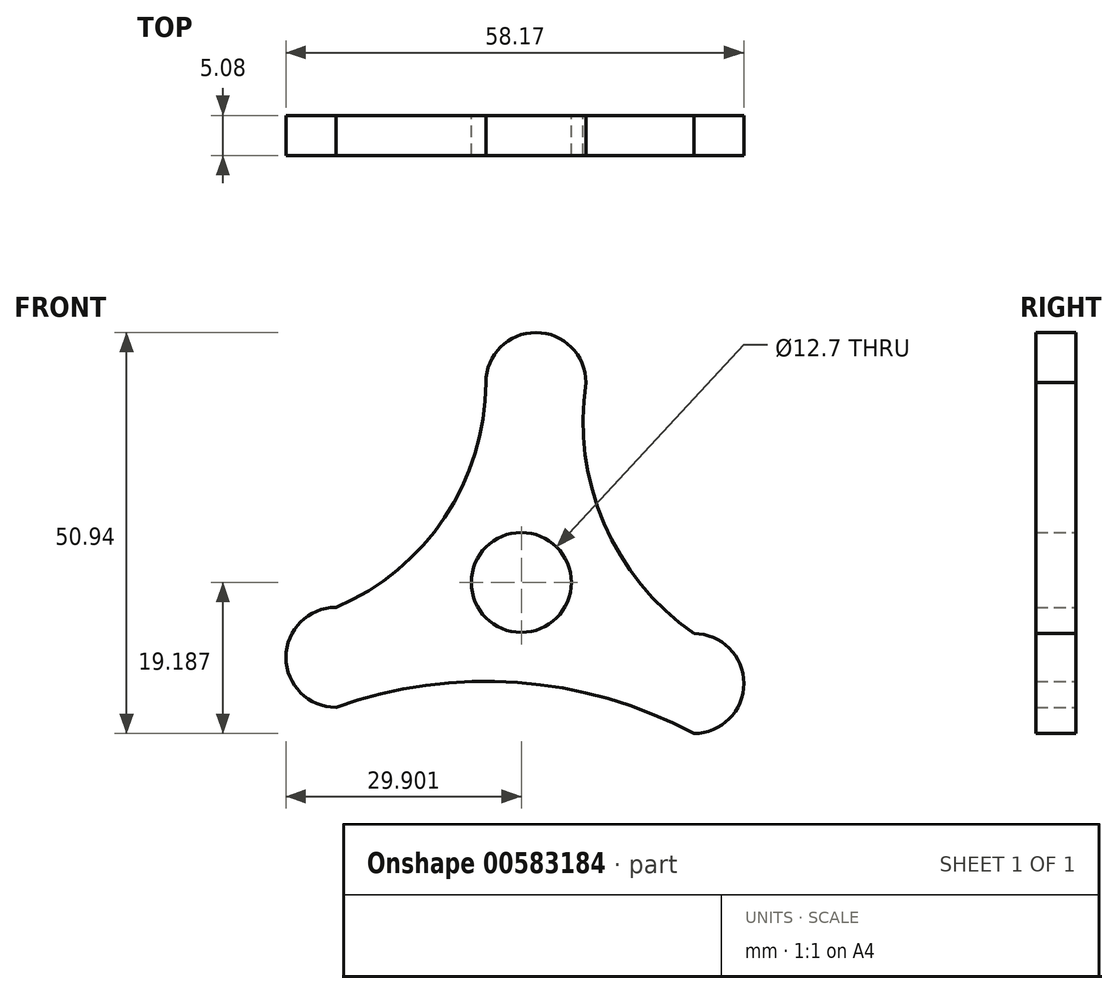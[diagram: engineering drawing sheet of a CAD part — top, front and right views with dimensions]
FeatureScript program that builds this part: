
annotation { "Feature Type Name" : "Feature", "Feature Type Description" : "" }
export const myFeature = defineFeature(function(context is Context, id is Id, definition is map)
    precondition{}
    {
        {
            var Q0;
            Q0=qCreatedBy(makeId("Front.planeOp"),FACE);
            var sketch = newSketch(context, id + "F0", { "sketchPlane" : qUnion([Q0])});
            skCircle(sketch, "E0", {"center": v(-49.79, 33.7) * mm, "radius": 6.35 * mm});
            skCircle(sketch, "E1", {"center": v(-47.93, 59.1) * mm, "radius": 6.35 * mm});
            skCircle(sketch, "E2", {"center": v(-27.87, 20.87) * mm, "radius": 6.35 * mm});
            skCircle(sketch, "E3", {"center": v(-73.34, 24.2) * mm, "radius": 6.35 * mm});
            skArc(sketch, "E4", {"start": v(-73.34, 30.54) * mm, "mid": v(-59.52, 41.96) * mm, "end": v(-54.28, 59.1) * mm});
            skArc(sketch, "E5", {"start": v(-41.58, 59.1) * mm, "mid": v(-39.28, 41.2) * mm, "end": v(-27.87, 27.22) * mm});
            skArc(sketch, "E6", {"start": v(-27.87, 14.52) * mm, "mid": v(-50.25, 21) * mm, "end": v(-73.34, 17.84) * mm});
            skSolve(sketch);
        }
        {
            var Q0;
            {var subQ0=sQuery(id+"F0.wireOp",EDGE,"E2");var subQ1=makeQuery(id+"F0.imprint","INTERSECT",VERTEX,{"derivedFrom":[subQ0,sQuery(id+"F0.wireOp",EDGE,"E5")]});Q0=makeQuery(id+"F0.imprint","IMPRINT",FACE,{"disambiguationData":[TD([[makeQuery(id+"F0.imprint","IMPRINT",EDGE,{"disambiguationData":[TD([[subQ1,-1.0]])],"derivedFrom":subQ0}),1.0]])]});}
            var Q1;
            Q1=makeQuery(id+"F0.imprint","IMPRINT",FACE,{"disambiguationData":[TD([[makeQuery(id+"F0.imprint","IMPRINT",EDGE,{"derivedFrom":sQuery(id+"F0.wireOp",EDGE,"E0")}),-1.0]])]});
            var Q2;
            {var subQ0=sQuery(id+"F0.wireOp",EDGE,"E3");var subQ1=makeQuery(id+"F0.imprint","INTERSECT",VERTEX,{"derivedFrom":[subQ0,sQuery(id+"F0.wireOp",EDGE,"E4")]});Q2=makeQuery(id+"F0.imprint","IMPRINT",FACE,{"disambiguationData":[TD([[makeQuery(id+"F0.imprint","IMPRINT",EDGE,{"disambiguationData":[TD([[subQ1,-1.0]])],"derivedFrom":subQ0}),1.0]])]});}
            var Q3;
            {var subQ0=sQuery(id+"F0.wireOp",EDGE,"E1");var subQ1=makeQuery(id+"F0.imprint","INTERSECT",VERTEX,{"derivedFrom":[subQ0,sQuery(id+"F0.wireOp",EDGE,"E4")]});Q3=makeQuery(id+"F0.imprint","IMPRINT",FACE,{"disambiguationData":[TD([[makeQuery(id+"F0.imprint","IMPRINT",EDGE,{"disambiguationData":[TD([[subQ1,1.0]])],"derivedFrom":subQ0}),1.0]])]});}
            extrude(context, id + "F1", {"entities" : qUnion([Q0, Q1, Q2, Q3]), "depth" : 5.08 * mm, "offsetDistance" : 25.4 * mm});
        }
    });
